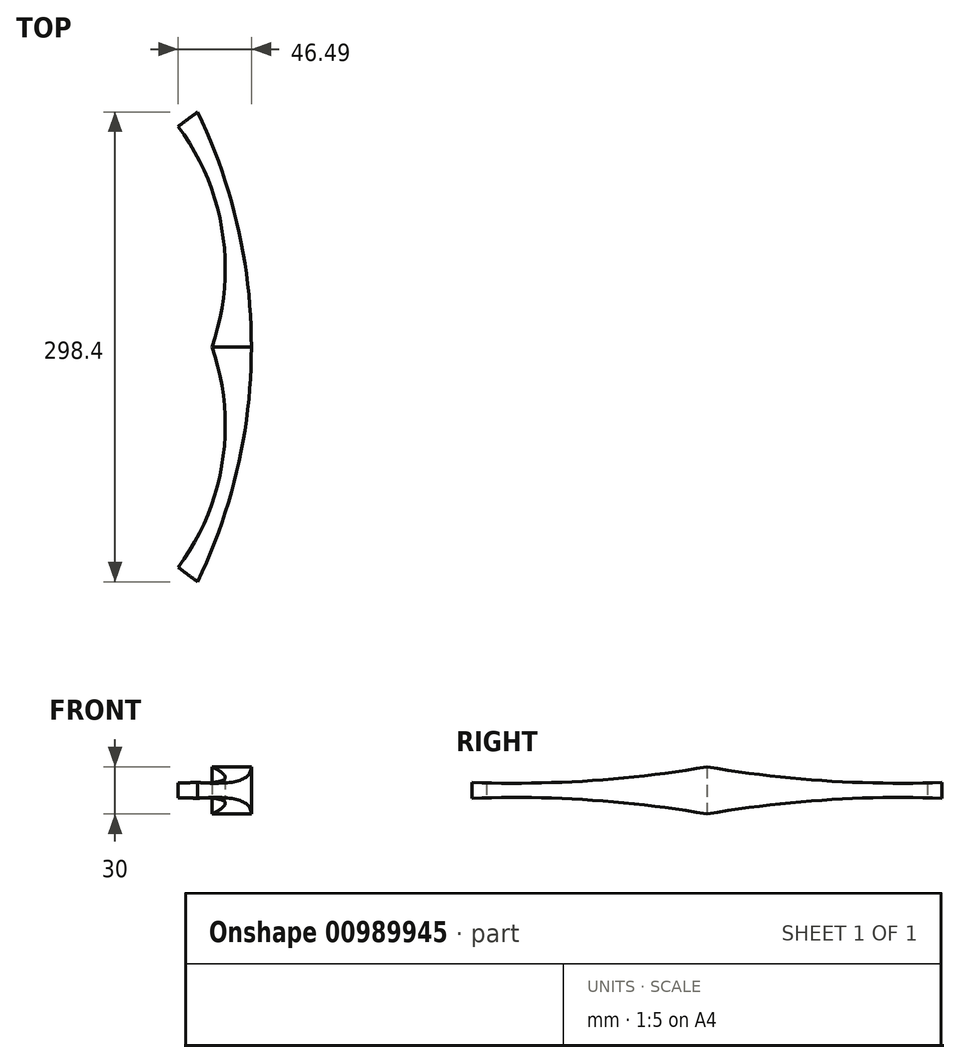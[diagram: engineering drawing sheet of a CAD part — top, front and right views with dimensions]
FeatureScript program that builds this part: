
annotation { "Feature Type Name" : "Feature", "Feature Type Description" : "" }
export const myFeature = defineFeature(function(context is Context, id is Id, definition is map)
    precondition{}
    {
        {
            var Q0;
            Q0=qCreatedBy(makeId("Top.planeOp"),FACE);
            var sketch = newSketch(context, id + "F0", { "sketchPlane" : qUnion([Q0])});
            skLineSegment(sketch, "E0", {"start": v(25, 0) * mm, "end": v(0, 0) * mm});
            skArc(sketch, "E1", {"start": v(0, 0) * mm, "mid": v(6.68, 72.68) * mm, "end": v(-21.49, 140.02) * mm});
            skArc(sketch, "E2", {"start": v(25, 0) * mm, "mid": v(16.35, 76.53) * mm, "end": v(-9.16, 149.2) * mm});
            skLineSegment(sketch, "E3", {"start": v(-9.16, 149.2) * mm, "end": v(-21.49, 140.02) * mm});
            skSolve(sketch);
        }
        {
            var Q0;
            Q0 = qSketchRegion(id + "F0", true);
            extrude(context, id + "F1", {"entities" : qUnion([Q0]), "depth" : 15 * mm, "offsetDistance" : 25 * mm});
        }
        {
            var Q0;
            Q0=qCreatedBy(makeId("Right.planeOp"),FACE);
            var sketch = newSketch(context, id + "F2", { "sketchPlane" : qUnion([Q0])});
            skArc(sketch, "E4", {"start": v(0, 15) * mm, "mid": v(74.34, 6.15) * mm, "end": v(149.2, 5.02) * mm});
            skLineSegment(sketch, "E5", {"start": v(149.2, 5.02) * mm, "end": v(149.2, 0) * mm});
            skLineSegment(sketch, "E6", {"start": v(149.2, 0) * mm, "end": v(0, 0) * mm});
            skLineSegment(sketch, "E7", {"start": v(0, 0) * mm, "end": v(0, 15) * mm});
            skSolve(sketch);
        }
        {
            var Q0;
            Q0 = qSketchRegion(id + "F2", true);
            extrude(context, id + "F3", {"entities" : qUnion([Q0]), "operationType" : NewBodyOperationType.INTERSECT, "endBound" : BoundingType.SYMMETRIC, "depth" : 60 * mm, "offsetDistance" : 25 * mm});
        }
        {
            var Q0;
            Q0=makeQuery(id+"F1.opExtrude","SWEPT_BODY",BODY,{"disambiguationData":[OSD([sQuery(id+"F0.wireOp",EDGE,"Fym3QENG-0o55-17oU-jROu-qLFDp7XCjcc8"),sQuery(id+"F0.wireOp",EDGE,"mBWvBnO1-YfqG-EvNb-E2Cb-frROlFpgnruP"),sQuery(id+"F0.wireOp",EDGE,"G1YH8ItU-pAkw-6zuw-GvgI-Zk1Hg34juM9N"),sQuery(id+"F0.wireOp",EDGE,"E0")])]});
            var Q1;
            Q1=qCreatedBy(makeId("Front.planeOp"),FACE);
            mirror(context, id + "F4", {"operationType" : NewBodyOperationType.ADD, "entities" : qUnion([Q0]), "mirrorPlane" : qUnion([Q1])});
        }
        {
            var Q0;
            Q0=makeQuery(id+"F1.opExtrude","SWEPT_BODY",BODY,{"disambiguationData":[OSD([sQuery(id+"F0.wireOp",EDGE,"Fym3QENG-0o55-17oU-jROu-qLFDp7XCjcc8"),sQuery(id+"F0.wireOp",EDGE,"mBWvBnO1-YfqG-EvNb-E2Cb-frROlFpgnruP"),sQuery(id+"F0.wireOp",EDGE,"G1YH8ItU-pAkw-6zuw-GvgI-Zk1Hg34juM9N"),sQuery(id+"F0.wireOp",EDGE,"E0")])]});
            var Q1;
            Q1=qCreatedBy(makeId("Top.planeOp"),FACE);
            mirror(context, id + "F5", {"operationType" : NewBodyOperationType.ADD, "entities" : qUnion([Q0]), "mirrorPlane" : qUnion([Q1])});
        }
    });
